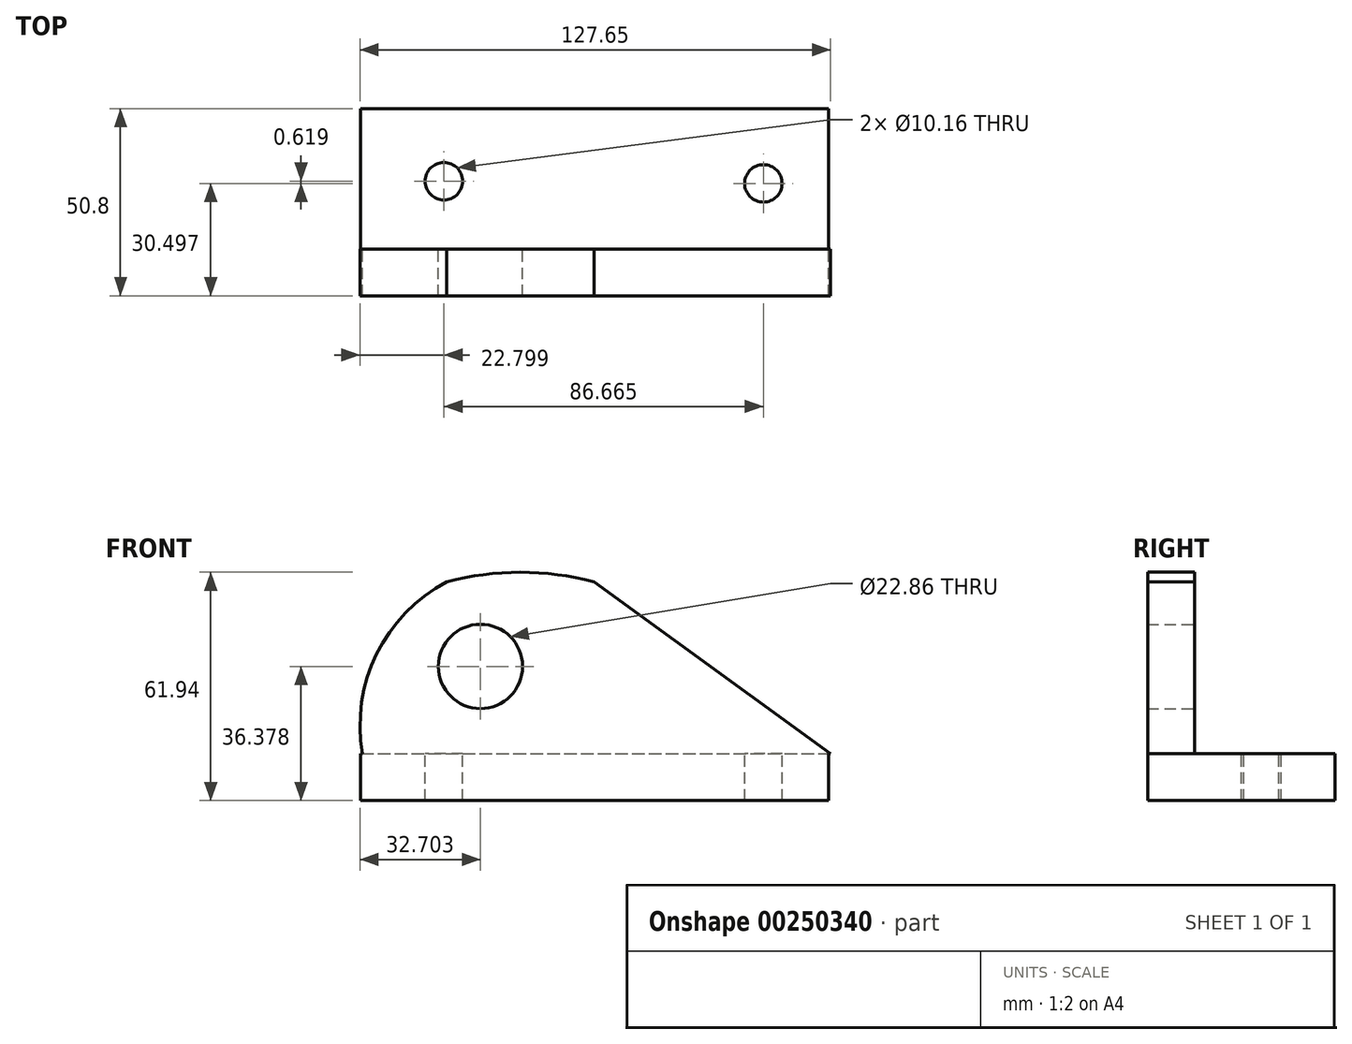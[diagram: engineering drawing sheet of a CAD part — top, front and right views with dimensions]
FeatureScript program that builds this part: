
annotation { "Feature Type Name" : "Feature", "Feature Type Description" : "" }
export const myFeature = defineFeature(function(context is Context, id is Id, definition is map)
    precondition{}
    {
        {
            var Q0;
            Q0=qCreatedBy(makeId("Front.planeOp"),FACE);
            var sketch = newSketch(context, id + "F0", { "sketchPlane" : qUnion([Q0])});
            skLineSegment(sketch, "E0", {"start": v(-50.45, 0) * mm, "end": v(76.55, 0) * mm});
            skArc(sketch, "E1", {"start": v(-27.55, 46.58) * mm, "mid": v(-46.57, 27.02) * mm, "end": v(-50.45, 0) * mm});
            skArc(sketch, "E2", {"start": v(12.38, 46.58) * mm, "mid": v(-7.58, 49.24) * mm, "end": v(-27.55, 46.58) * mm});
            skLineSegment(sketch, "E3", {"start": v(12.38, 46.58) * mm, "end": v(76.55, 0) * mm});
            skSolve(sketch);
        }
        {
            var Q0;
            Q0 = qSketchRegion(id + "F0", true);
            extrude(context, id + "F1", {"entities" : qUnion([Q0]), "depth" : 12.7 * mm});
        }
        {
            var Q0;
            Q0=qCreatedBy(makeId("Front.planeOp"),FACE);
            var sketch = newSketch(context, id + "F2", { "sketchPlane" : qUnion([Q0])});
            skLineSegment(sketch, "E4.bottom", {"start": v(-50.9, 0) * mm, "end": v(76.1, 0) * mm});
            skLineSegment(sketch, "E4.top", {"start": v(-50.9, -12.7) * mm, "end": v(76.1, -12.7) * mm});
            skLineSegment(sketch, "E4.left", {"start": v(-50.9, 0) * mm, "end": v(-50.9, -12.7) * mm});
            skLineSegment(sketch, "E4.right", {"start": v(76.1, 0) * mm, "end": v(76.1, -12.7) * mm});
            skSolve(sketch);
        }
        {
            var Q0;
            Q0 = qSketchRegion(id + "F2", true);
            extrude(context, id + "F3", {"entities" : qUnion([Q0]), "operationType" : NewBodyOperationType.ADD, "depth" : 12.7 * mm, "hasSecondDirection" : true, "secondDirectionOppositeDirection" : true, "secondDirectionDepth" : 38.1 * mm});
        }
        {
            var Q0;
            Q0=qCreatedBy(makeId("Top.planeOp"),FACE);
            var sketch = newSketch(context, id + "F4", { "sketchPlane" : qUnion([Q0])});
            skCircle(sketch, "E5", {"center": v(-28.3, 18.42) * mm, "radius": 4.76 * mm});
            skCircle(sketch, "E6", {"center": v(58.36, 17.8) * mm, "radius": 4.76 * mm});
            skSolve(sketch);
        }
        {
            var Q0;
            Q0=sQuery(id+"F4.wireOp",VERTEX,"E5.center");
            var Q1;
            Q1=sQuery(id+"F4.wireOp",VERTEX,"E6.center");
            var Q2;
            Q2=makeQuery(id+"F1.opExtrude","SWEPT_BODY",BODY,{"disambiguationData":[OSD([sQuery(id+"F0.wireOp",EDGE,"E0"),sQuery(id+"F0.wireOp",EDGE,"E1"),sQuery(id+"F0.wireOp",EDGE,"E2"),sQuery(id+"F0.wireOp",EDGE,"E3")])]});
            hole(context, id + "F5", {"style" : HoleStyle.SIMPLE, "endStyle" : HoleEndStyle.THROUGH, "holeDiameter" : 10.16 * mm, "tappedDepth" : 12.7 * mm, "tapClearance" : 3, "locations" : qUnion([Q0, Q1]), "scope" : qUnion([Q2])});
        }
        {
            var Q0;
            Q0=qCreatedBy(makeId("Front.planeOp"),FACE);
            var sketch = newSketch(context, id + "F6", { "sketchPlane" : qUnion([Q0])});
            skCircle(sketch, "E7", {"center": v(-18.4, 23.68) * mm, "radius": 11.11 * mm});
            skSolve(sketch);
        }
        {
            var Q0;
            Q0=sQuery(id+"F6.wireOp",VERTEX,"E7.center");
            var Q1;
            Q1=makeQuery(id+"F1.opExtrude","SWEPT_BODY",BODY,{"disambiguationData":[OSD([sQuery(id+"F0.wireOp",EDGE,"E0"),sQuery(id+"F0.wireOp",EDGE,"E1"),sQuery(id+"F0.wireOp",EDGE,"E2"),sQuery(id+"F0.wireOp",EDGE,"E3")])]});
            hole(context, id + "F7", {"style" : HoleStyle.SIMPLE, "endStyle" : HoleEndStyle.THROUGH, "oppositeDirection" : true, "holeDiameter" : 22.86 * mm, "tappedDepth" : 12.7 * mm, "tapClearance" : 3, "locations" : qUnion([Q0]), "scope" : qUnion([Q1])});
        }
    });
